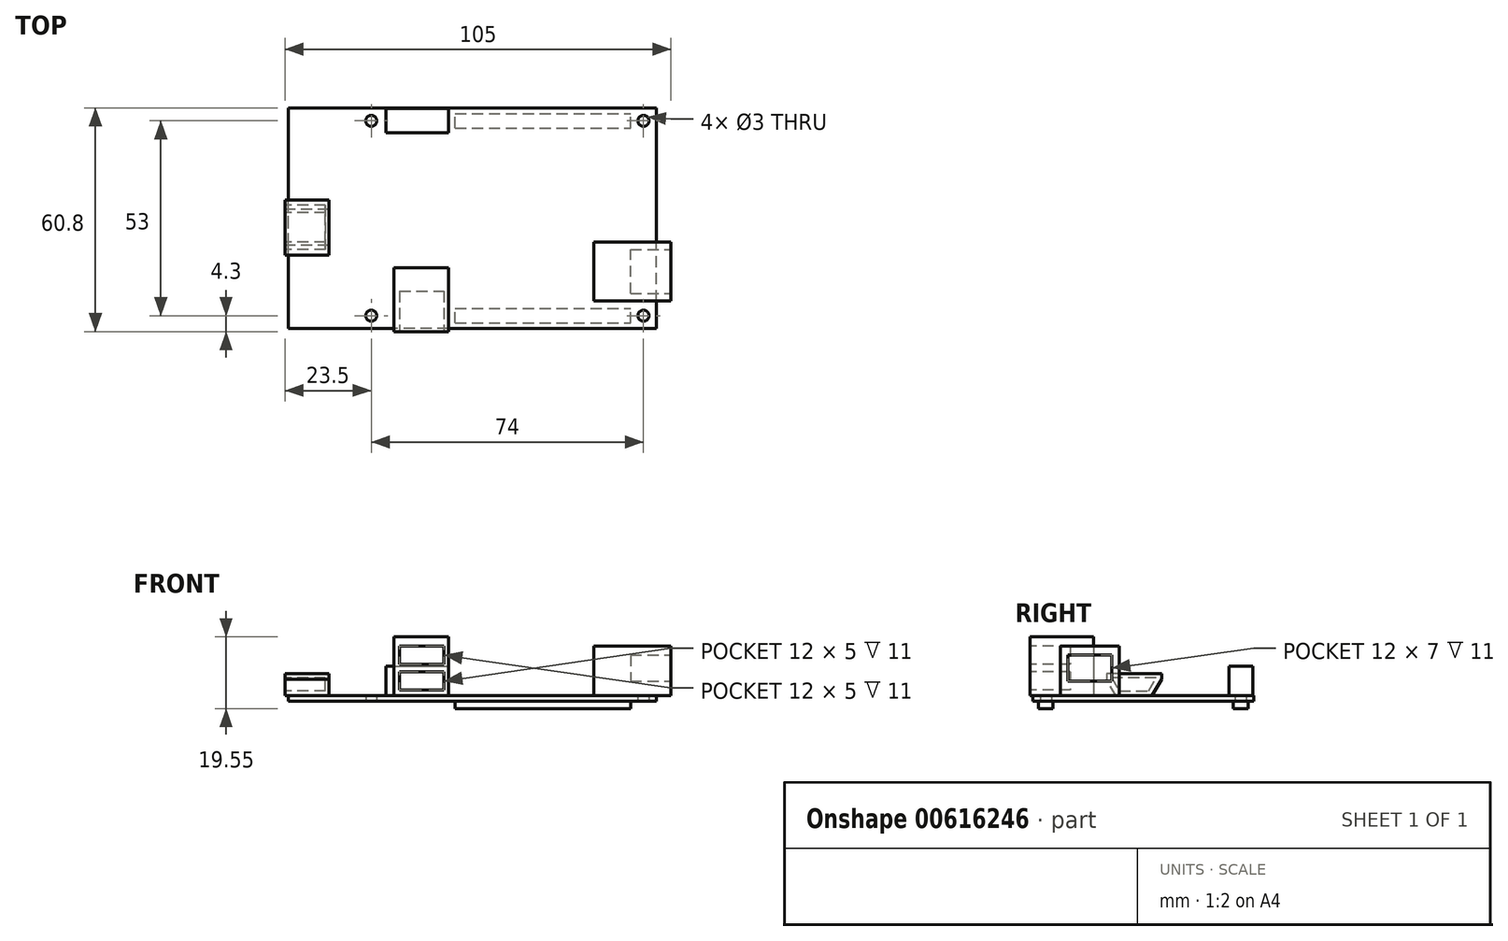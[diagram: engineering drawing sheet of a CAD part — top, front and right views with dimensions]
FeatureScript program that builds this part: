
annotation { "Feature Type Name" : "Feature", "Feature Type Description" : "" }
export const myFeature = defineFeature(function(context is Context, id is Id, definition is map)
    precondition{}
    {
        {
            var Q0;
            Q0=qCreatedBy(makeId("Top.planeOp"),FACE);
            var sketch = newSketch(context, id + "F0", { "sketchPlane" : qUnion([Q0])});
            skLineSegment(sketch, "E0.bottom", {"start": v(50, -30) * mm, "end": v(-50, -30) * mm});
            skLineSegment(sketch, "E0.top", {"start": v(50, 30) * mm, "end": v(-50, 30) * mm});
            skLineSegment(sketch, "E0.left", {"start": v(50, -30) * mm, "end": v(50, 30) * mm});
            skLineSegment(sketch, "E0.right", {"start": v(-50, -30) * mm, "end": v(-50, 30) * mm});
            skPoint(sketch, "E0.middle", {"position": v(0, 0) * mm});
            skCircle(sketch, "E1", {"center": v(-27.5, 26.5) * mm, "radius": 1.5 * mm});
            skCircle(sketch, "E2", {"center": v(46.5, 26.5) * mm, "radius": 1.5 * mm});
            skCircle(sketch, "E3", {"center": v(46.5, -26.5) * mm, "radius": 1.5 * mm});
            skCircle(sketch, "E4", {"center": v(-27.5, -26.5) * mm, "radius": 1.5 * mm});
            skLineSegment(sketch, "E5", {"start": v(-63.69, 26.5) * mm, "end": v(62.57, 26.5) * mm, "construction": true});
            skLineSegment(sketch, "E6", {"start": v(46.5, 41.66) * mm, "end": v(46.5, -41.34) * mm, "construction": true});
            skLineSegment(sketch, "E7", {"start": v(71.38, -26.5) * mm, "end": v(-68.5, -26.5) * mm, "construction": true});
            skLineSegment(sketch, "E8", {"start": v(-27.5, 41.66) * mm, "end": v(-27.5, -33.97) * mm, "construction": true});
            skSolve(sketch);
        }
        {
            var Q0;
            Q0=makeQuery(id+"F0.imprint","IMPRINT",FACE,{"disambiguationData":[TD([[makeQuery(id+"F0.imprint","IMPRINT",EDGE,{"derivedFrom":sQuery(id+"F0.wireOp",EDGE,"E0.bottom")}),-1.0]])]});
            extrude(context, id + "F1", {"entities" : qUnion([Q0]), "depth" : 1.55 * mm, "offsetDistance" : 25 * mm});
        }
        {
            var Q0;
            Q0=makeQuery(id+"F1.opExtrude","CAP_FACE",FACE,{"disambiguationData":[OSD([sQuery(id+"F0.wireOp",EDGE,"E0.bottom"),sQuery(id+"F0.wireOp",EDGE,"E0.top"),sQuery(id+"F0.wireOp",EDGE,"E0.left"),sQuery(id+"F0.wireOp",EDGE,"E0.right"),sQuery(id+"F0.wireOp",EDGE,"E1"),sQuery(id+"F0.wireOp",EDGE,"E2"),sQuery(id+"F0.wireOp",EDGE,"E3"),sQuery(id+"F0.wireOp",EDGE,"E4")])],"isStart":false});
            var sketch = newSketch(context, id + "F2", { "sketchPlane" : qUnion([Q0])});
            skLineSegment(sketch, "E9.bottom", {"start": v(33, -6.5) * mm, "end": v(54, -6.5) * mm});
            skLineSegment(sketch, "E9.top", {"start": v(33, -22.5) * mm, "end": v(54, -22.5) * mm});
            skLineSegment(sketch, "E9.left", {"start": v(33, -6.5) * mm, "end": v(33, -22.5) * mm});
            skLineSegment(sketch, "E9.right", {"start": v(54, -6.5) * mm, "end": v(54, -22.5) * mm});
            skSolve(sketch);
        }
        {
            var Q0;
            {var subQ0=sQuery(id+"F2.wireOp",EDGE,"E9.left");Q0=makeQuery(id+"F2.imprint","IMPRINT",FACE,{"disambiguationData":[TD([[makeQuery(id+"F2.imprint","IMPRINT",EDGE,{"derivedFrom":subQ0}),1.0]])]});}
            var Q1;
            {var subQ0=sQuery(id+"F2.wireOp",EDGE,"E9.right");Q1=makeQuery(id+"F2.imprint","IMPRINT",FACE,{"disambiguationData":[TD([[makeQuery(id+"F2.imprint","IMPRINT",EDGE,{"derivedFrom":subQ0}),-1.0]])]});}
            extrude(context, id + "F3", {"entities" : qUnion([Q0, Q1]), "operationType" : NewBodyOperationType.ADD, "depth" : 13.5 * mm, "offsetDistance" : 25 * mm});
        }
        {
            var Q0;
            Q0=makeQuery(id+"F1.opExtrude","CAP_FACE",FACE,{"disambiguationData":[OSD([sQuery(id+"F0.wireOp",EDGE,"E0.bottom"),sQuery(id+"F0.wireOp",EDGE,"E0.top"),sQuery(id+"F0.wireOp",EDGE,"E0.left"),sQuery(id+"F0.wireOp",EDGE,"E0.right"),sQuery(id+"F0.wireOp",EDGE,"E1"),sQuery(id+"F0.wireOp",EDGE,"E2"),sQuery(id+"F0.wireOp",EDGE,"E3"),sQuery(id+"F0.wireOp",EDGE,"E4")])],"isStart":false});
            var sketch = newSketch(context, id + "F4", { "sketchPlane" : qUnion([Q0])});
            skLineSegment(sketch, "E10.bottom", {"start": v(-21.3, -13.5) * mm, "end": v(-6.5, -13.5) * mm});
            skLineSegment(sketch, "E10.top", {"start": v(-21.3, -30.8) * mm, "end": v(-6.5, -30.8) * mm});
            skLineSegment(sketch, "E10.left", {"start": v(-21.3, -13.5) * mm, "end": v(-21.3, -30.8) * mm});
            skLineSegment(sketch, "E10.right", {"start": v(-6.5, -13.5) * mm, "end": v(-6.5, -30.8) * mm});
            skSolve(sketch);
        }
        {
            var Q0;
            {var subQ0=sQuery(id+"F4.wireOp",EDGE,"E10.bottom");Q0=makeQuery(id+"F4.imprint","IMPRINT",FACE,{"disambiguationData":[TD([[makeQuery(id+"F4.imprint","IMPRINT",EDGE,{"derivedFrom":subQ0}),-1.0]])]});}
            var Q1;
            {var subQ0=sQuery(id+"F4.wireOp",EDGE,"E10.top");Q1=makeQuery(id+"F4.imprint","IMPRINT",FACE,{"disambiguationData":[TD([[makeQuery(id+"F4.imprint","IMPRINT",EDGE,{"derivedFrom":subQ0}),1.0]])]});}
            extrude(context, id + "F5", {"entities" : qUnion([Q0, Q1]), "operationType" : NewBodyOperationType.ADD, "depth" : 16 * mm, "offsetDistance" : 25 * mm});
        }
        {
            var Q0;
            Q0=makeQuery(id+"F1.opExtrude","CAP_FACE",FACE,{"disambiguationData":[OSD([sQuery(id+"F0.wireOp",EDGE,"E0.bottom"),sQuery(id+"F0.wireOp",EDGE,"E0.top"),sQuery(id+"F0.wireOp",EDGE,"E0.left"),sQuery(id+"F0.wireOp",EDGE,"E0.right"),sQuery(id+"F0.wireOp",EDGE,"E1"),sQuery(id+"F0.wireOp",EDGE,"E2"),sQuery(id+"F0.wireOp",EDGE,"E3"),sQuery(id+"F0.wireOp",EDGE,"E4")])],"isStart":true});
            var sketch = newSketch(context, id + "F6", { "sketchPlane" : qUnion([Q0])});
            skLineSegment(sketch, "E11.bottom", {"start": v(-4.7, 28.5) * mm, "end": v(43, 28.5) * mm});
            skLineSegment(sketch, "E11.top", {"start": v(-4.7, 24.5) * mm, "end": v(43, 24.5) * mm});
            skLineSegment(sketch, "E11.left", {"start": v(-4.7, 28.5) * mm, "end": v(-4.7, 24.5) * mm});
            skLineSegment(sketch, "E11.right", {"start": v(43, 28.5) * mm, "end": v(43, 24.5) * mm});
            skLineSegment(sketch, "E12.bottom", {"start": v(-4.7, -24.5) * mm, "end": v(43, -24.5) * mm});
            skLineSegment(sketch, "E12.top", {"start": v(-4.7, -28.5) * mm, "end": v(43, -28.5) * mm});
            skLineSegment(sketch, "E12.left", {"start": v(-4.7, -24.5) * mm, "end": v(-4.7, -28.5) * mm});
            skLineSegment(sketch, "E12.right", {"start": v(43, -24.5) * mm, "end": v(43, -28.5) * mm});
            skSolve(sketch);
        }
        {
            var Q0;
            Q0=makeQuery(id+"F6.imprint","IMPRINT",FACE,{"disambiguationData":[TD([[makeQuery(id+"F6.imprint","IMPRINT",EDGE,{"derivedFrom":sQuery(id+"F6.wireOp",EDGE,"E11.bottom")}),-1.0]])]});
            var Q1;
            Q1=makeQuery(id+"F6.imprint","IMPRINT",FACE,{"disambiguationData":[TD([[makeQuery(id+"F6.imprint","IMPRINT",EDGE,{"derivedFrom":sQuery(id+"F6.wireOp",EDGE,"E12.bottom")}),-1.0]])]});
            extrude(context, id + "F7", {"entities" : qUnion([Q0, Q1]), "operationType" : NewBodyOperationType.ADD, "depth" : 2 * mm, "offsetDistance" : 25 * mm});
        }
        {
            var Q0;
            Q0=makeQuery(id+"F1.opExtrude","CAP_FACE",FACE,{"disambiguationData":[OSD([sQuery(id+"F0.wireOp",EDGE,"E0.bottom"),sQuery(id+"F0.wireOp",EDGE,"E0.top"),sQuery(id+"F0.wireOp",EDGE,"E0.left"),sQuery(id+"F0.wireOp",EDGE,"E0.right"),sQuery(id+"F0.wireOp",EDGE,"E1"),sQuery(id+"F0.wireOp",EDGE,"E2"),sQuery(id+"F0.wireOp",EDGE,"E3"),sQuery(id+"F0.wireOp",EDGE,"E4")])],"isStart":false});
            var sketch = newSketch(context, id + "F8", { "sketchPlane" : qUnion([Q0])});
            skLineSegment(sketch, "E13.bottom", {"start": v(-23.5, 29.8) * mm, "end": v(-6.5, 29.8) * mm});
            skLineSegment(sketch, "E13.top", {"start": v(-23.5, 23.3) * mm, "end": v(-6.5, 23.3) * mm});
            skLineSegment(sketch, "E13.left", {"start": v(-23.5, 29.8) * mm, "end": v(-23.5, 23.3) * mm});
            skLineSegment(sketch, "E13.right", {"start": v(-6.5, 29.8) * mm, "end": v(-6.5, 23.3) * mm});
            skSolve(sketch);
        }
        {
            var Q0;
            Q0=makeQuery(id+"F8.imprint","IMPRINT",FACE,{"disambiguationData":[TD([[makeQuery(id+"F8.imprint","IMPRINT",EDGE,{"derivedFrom":sQuery(id+"F8.wireOp",EDGE,"E13.bottom")}),-1.0]])]});
            extrude(context, id + "F9", {"entities" : qUnion([Q0]), "operationType" : NewBodyOperationType.ADD, "depth" : 8 * mm, "offsetDistance" : 25 * mm});
        }
        {
            var Q0;
            Q0=makeQuery(id+"F1.opExtrude","CAP_FACE",FACE,{"disambiguationData":[OSD([sQuery(id+"F0.wireOp",EDGE,"E0.bottom"),sQuery(id+"F0.wireOp",EDGE,"E0.top"),sQuery(id+"F0.wireOp",EDGE,"E0.left"),sQuery(id+"F0.wireOp",EDGE,"E0.right"),sQuery(id+"F0.wireOp",EDGE,"E1"),sQuery(id+"F0.wireOp",EDGE,"E2"),sQuery(id+"F0.wireOp",EDGE,"E3"),sQuery(id+"F0.wireOp",EDGE,"E4")])],"isStart":false});
            var sketch = newSketch(context, id + "F10", { "sketchPlane" : qUnion([Q0])});
            skLineSegment(sketch, "E14.bottom", {"start": v(-51, 5) * mm, "end": v(-39, 5) * mm});
            skLineSegment(sketch, "E14.top", {"start": v(-51, -10) * mm, "end": v(-39, -10) * mm});
            skLineSegment(sketch, "E14.left", {"start": v(-51, 5) * mm, "end": v(-51, -10) * mm});
            skLineSegment(sketch, "E14.right", {"start": v(-39, 5) * mm, "end": v(-39, -10) * mm});
            skSolve(sketch);
        }
        {
            var Q0;
            {var subQ0=sQuery(id+"F10.wireOp",EDGE,"E14.right");Q0=makeQuery(id+"F10.imprint","IMPRINT",FACE,{"disambiguationData":[TD([[makeQuery(id+"F10.imprint","IMPRINT",EDGE,{"derivedFrom":subQ0}),-1.0]])]});}
            var Q1;
            {var subQ0=sQuery(id+"F10.wireOp",EDGE,"E14.left");Q1=makeQuery(id+"F10.imprint","IMPRINT",FACE,{"disambiguationData":[TD([[makeQuery(id+"F10.imprint","IMPRINT",EDGE,{"derivedFrom":subQ0}),1.0]])]});}
            extrude(context, id + "F11", {"entities" : qUnion([Q0, Q1]), "operationType" : NewBodyOperationType.ADD, "depth" : 6 * mm, "offsetDistance" : 25 * mm});
        }
        {
            var Q0;
            Q0=makeQuery(id+"F3.opExtrude","SWEPT_FACE",FACE,{"disambiguationData":[OSD([sQuery(id+"F2.wireOp",EDGE,"E9.right")])]});
            var sketch = newSketch(context, id + "F12", { "sketchPlane" : qUnion([Q0])});
            skLineSegment(sketch, "E15.bottom", {"start": v(-20.5, 12.55) * mm, "end": v(-8.5, 12.55) * mm});
            skLineSegment(sketch, "E15.top", {"start": v(-20.5, 5.55) * mm, "end": v(-8.5, 5.55) * mm});
            skLineSegment(sketch, "E15.left", {"start": v(-20.5, 12.55) * mm, "end": v(-20.5, 5.55) * mm});
            skLineSegment(sketch, "E15.right", {"start": v(-8.5, 12.55) * mm, "end": v(-8.5, 5.55) * mm});
            skLineSegment(sketch, "E16.bottom", {"start": v(-17.65, 5.55) * mm, "end": v(-11.35, 5.55) * mm});
            skLineSegment(sketch, "E16.top", {"start": v(-17.65, 3.55) * mm, "end": v(-11.35, 3.55) * mm});
            skLineSegment(sketch, "E16.left", {"start": v(-17.65, 5.55) * mm, "end": v(-17.65, 3.55) * mm});
            skLineSegment(sketch, "E16.right", {"start": v(-11.35, 5.55) * mm, "end": v(-11.35, 3.55) * mm});
            skSolve(sketch);
        }
        {
            var Q0;
            Q0=makeQuery(id+"F12.imprint","IMPRINT",FACE,{"disambiguationData":[TD([[makeQuery(id+"F12.imprint","IMPRINT",EDGE,{"derivedFrom":sQuery(id+"F12.wireOp",EDGE,"E15.bottom")}),-1.0]])]});
            var Q1;
            Q1=makeQuery(id+"F12.imprint","IMPRINT",FACE,{"disambiguationData":[TD([[makeQuery(id+"F12.imprint","IMPRINT",EDGE,{"derivedFrom":sQuery(id+"F12.wireOp",EDGE,"E16.bottom")}),-1.0]])]});
            extrude(context, id + "F13", {"entities" : qUnion([Q0, Q1]), "operationType" : NewBodyOperationType.REMOVE, "oppositeDirection" : true, "depth" : 11 * mm, "offsetDistance" : 25 * mm});
        }
        {
            var Q0;
            Q0=makeQuery(id+"F5.opExtrude","SWEPT_FACE",FACE,{"disambiguationData":[OSD([sQuery(id+"F4.wireOp",EDGE,"E10.top")])]});
            var sketch = newSketch(context, id + "F14", { "sketchPlane" : qUnion([Q0])});
            skLineSegment(sketch, "E17.bottom", {"start": v(-19.8, 15.05) * mm, "end": v(-7.8, 15.05) * mm});
            skLineSegment(sketch, "E17.top", {"start": v(-19.8, 10.05) * mm, "end": v(-7.8, 10.05) * mm});
            skLineSegment(sketch, "E17.left", {"start": v(-19.8, 15.05) * mm, "end": v(-19.8, 10.05) * mm});
            skLineSegment(sketch, "E17.right", {"start": v(-7.8, 15.05) * mm, "end": v(-7.8, 10.05) * mm});
            skLineSegment(sketch, "E18.bottom", {"start": v(-19.8, 8.05) * mm, "end": v(-7.8, 8.05) * mm});
            skLineSegment(sketch, "E18.top", {"start": v(-19.8, 3.05) * mm, "end": v(-7.8, 3.05) * mm});
            skLineSegment(sketch, "E18.left", {"start": v(-19.8, 8.05) * mm, "end": v(-19.8, 3.05) * mm});
            skLineSegment(sketch, "E18.right", {"start": v(-7.8, 8.05) * mm, "end": v(-7.8, 3.05) * mm});
            skSolve(sketch);
        }
        {
            var Q0;
            Q0=makeQuery(id+"F14.imprint","IMPRINT",FACE,{"disambiguationData":[TD([[makeQuery(id+"F14.imprint","IMPRINT",EDGE,{"derivedFrom":sQuery(id+"F14.wireOp",EDGE,"E17.bottom")}),-1.0]])]});
            var Q1;
            Q1=makeQuery(id+"F14.imprint","IMPRINT",FACE,{"disambiguationData":[TD([[makeQuery(id+"F14.imprint","IMPRINT",EDGE,{"derivedFrom":sQuery(id+"F14.wireOp",EDGE,"E18.bottom")}),-1.0]])]});
            extrude(context, id + "F15", {"entities" : qUnion([Q0, Q1]), "operationType" : NewBodyOperationType.REMOVE, "oppositeDirection" : true, "depth" : 11 * mm, "offsetDistance" : 25 * mm});
        }
        {
            var Q0;
            Q0=makeQuery(id+"F11.opExtrude","SWEPT_FACE",FACE,{"disambiguationData":[OSD([sQuery(id+"F10.wireOp",EDGE,"E14.left")])]});
            var sketch = newSketch(context, id + "F16", { "sketchPlane" : qUnion([Q0])});
            skLineSegment(sketch, "E19", {"start": v(-3.5, 6.35) * mm, "end": v(8.5, 6.35) * mm});
            skLineSegment(sketch, "E20", {"start": v(8.5, 6.35) * mm, "end": v(6.5, 2.85) * mm});
            skLineSegment(sketch, "E21", {"start": v(6.5, 2.85) * mm, "end": v(-1.5, 2.85) * mm});
            skLineSegment(sketch, "E22", {"start": v(-1.5, 2.85) * mm, "end": v(-3.5, 6.35) * mm});
            skSolve(sketch);
        }
        {
            var Q0;
            Q0=makeQuery(id+"F16.imprint","IMPRINT",FACE,{"disambiguationData":[TD([[makeQuery(id+"F16.imprint","IMPRINT",EDGE,{"derivedFrom":sQuery(id+"F16.wireOp",EDGE,"E19")}),-1.0]])]});
            extrude(context, id + "F17", {"entities" : qUnion([Q0]), "operationType" : NewBodyOperationType.REMOVE, "oppositeDirection" : true, "depth" : 11 * mm, "offsetDistance" : 25 * mm});
        }
        {
            var Q0;
            Q0=makeQuery(id+"F11.opExtrude","SWEPT_FACE",FACE,{"disambiguationData":[OSD([sQuery(id+"F10.wireOp",EDGE,"E14.left")])]});
            var sketch = newSketch(context, id + "F18", { "sketchPlane" : qUnion([Q0])});
            skLineSegment(sketch, "E23", {"start": v(7.42, 1.55) * mm, "end": v(10, 6.06) * mm});
            skLineSegment(sketch, "E24", {"start": v(-2.42, 1.55) * mm, "end": v(-5, 6.06) * mm});
            skSolve(sketch);
        }
        {
            var Q0;
            {var subQ0=sQuery(id+"F18.wireOp",EDGE,"E23");Q0=makeQuery(id+"F18.imprint","IMPRINT",FACE,{"disambiguationData":[TD([[makeQuery(id+"F18.imprint","IMPRINT",EDGE,{"derivedFrom":subQ0}),-1.0]])]});}
            var Q1;
            {var subQ0=sQuery(id+"F18.wireOp",EDGE,"E24");Q1=makeQuery(id+"F18.imprint","IMPRINT",FACE,{"disambiguationData":[TD([[makeQuery(id+"F18.imprint","IMPRINT",EDGE,{"derivedFrom":subQ0}),1.0]])]});}
            extrude(context, id + "F19", {"entities" : qUnion([Q0, Q1]), "operationType" : NewBodyOperationType.REMOVE, "endBound" : BoundingType.UP_TO_NEXT, "oppositeDirection" : true, "depth" : 25 * mm, "offsetDistance" : 25 * mm});
        }
    });
